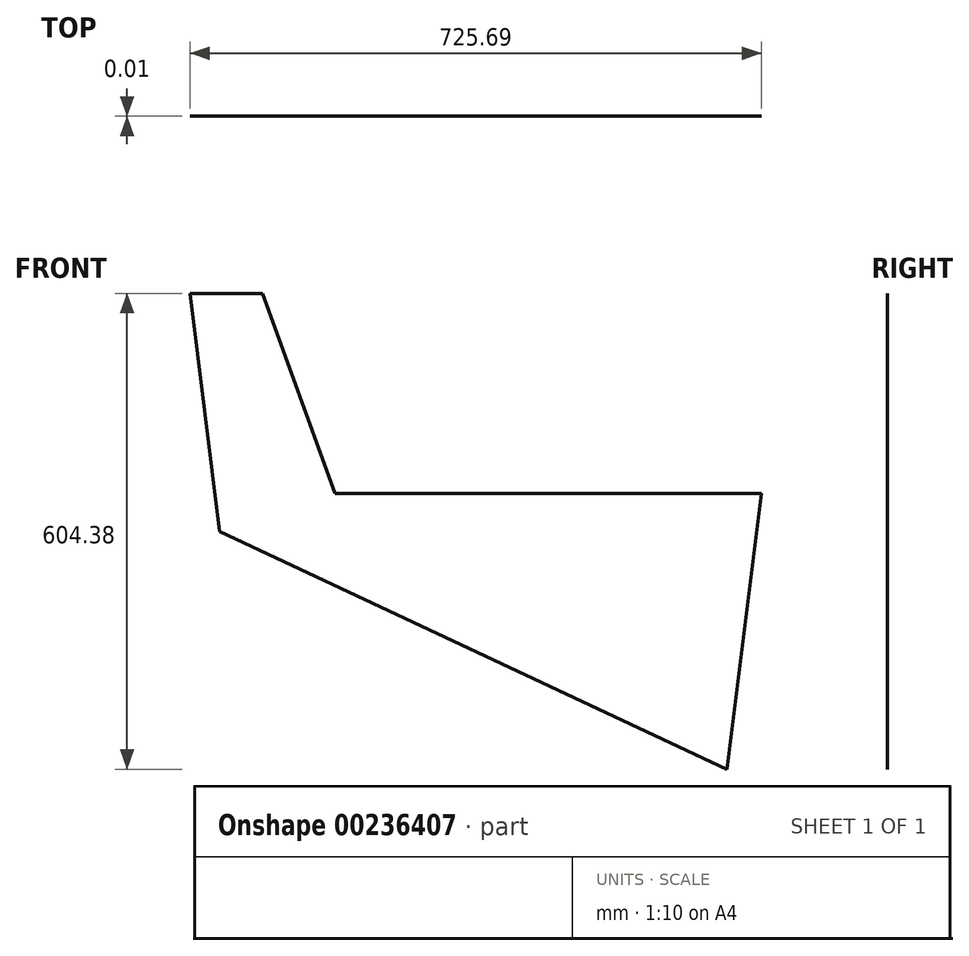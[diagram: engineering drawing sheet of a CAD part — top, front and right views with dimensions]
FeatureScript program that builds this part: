
annotation { "Feature Type Name" : "Feature", "Feature Type Description" : "" }
export const myFeature = defineFeature(function(context is Context, id is Id, definition is map)
    precondition{}
    {
        {
            var Q0;
            Q0=qCreatedBy(makeId("Front.planeOp"),FACE);
            var sketch = newSketch(context, id + "F0", { "sketchPlane" : qUnion([Q0])});
            skLineSegment(sketch, "E0", {"start": v(-286.97, 235.81) * mm, "end": v(-249.45, -66.67) * mm});
            skLineSegment(sketch, "E1", {"start": v(-249.45, -66.67) * mm, "end": v(395.27, -368.57) * mm});
            skLineSegment(sketch, "E2", {"start": v(395.27, -368.57) * mm, "end": v(438.72, -18.19) * mm});
            skLineSegment(sketch, "E3", {"start": v(-195, 235.81) * mm, "end": v(-286.97, 235.81) * mm});
            skLineSegment(sketch, "E4", {"start": v(438.72, -18.19) * mm, "end": v(-102.56, -18.19) * mm});
            skLineSegment(sketch, "E5", {"start": v(-102.56, -18.19) * mm, "end": v(-195, 235.81) * mm});
            skSolve(sketch);
        }
        {
            var Q0;
            Q0 = qSketchRegion(id + "F0", true);
            extrude(context, id + "F1", {"entities" : qUnion([Q0]), "depth" : 3 / 406.4 * mm});
        }
    });
